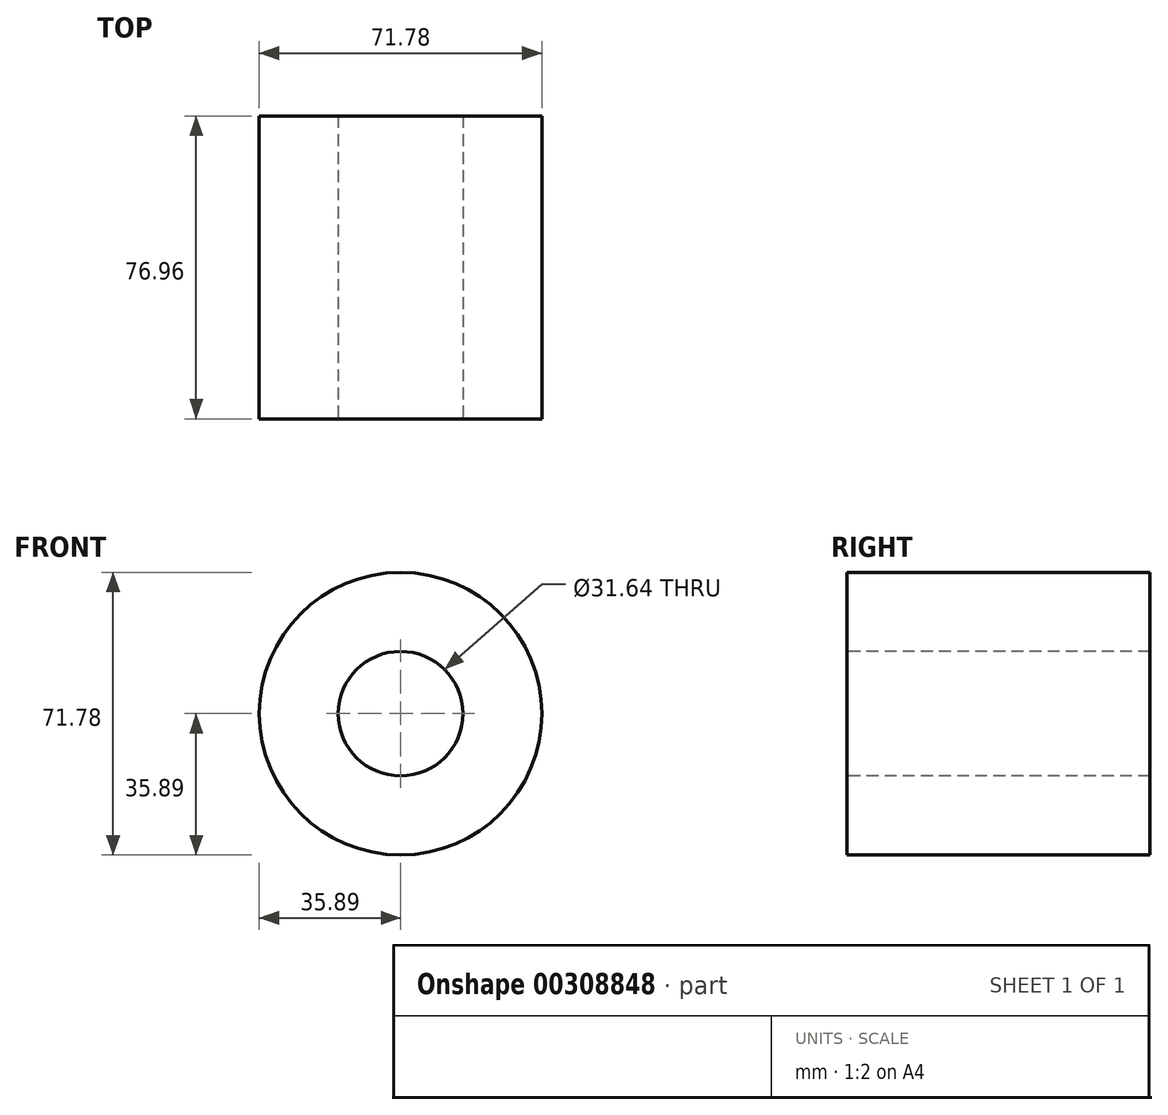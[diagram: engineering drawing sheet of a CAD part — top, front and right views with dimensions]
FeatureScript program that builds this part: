
annotation { "Feature Type Name" : "Feature", "Feature Type Description" : "" }
export const myFeature = defineFeature(function(context is Context, id is Id, definition is map)
    precondition{}
    {
        {
            var Q0;
            Q0=qCreatedBy(makeId("Front.planeOp"),FACE);
            var sketch = newSketch(context, id + "F0", { "sketchPlane" : qUnion([Q0])});
            skCircle(sketch, "E0", {"center": v(0, 0) * mm, "radius": 35.9 * mm});
            skSolve(sketch);
        }
        {
            var Q0;
            Q0=makeQuery(id+"F0.imprint","IMPRINT",FACE,{"disambiguationData":[TD([[makeQuery(id+"F0.imprint","IMPRINT",EDGE,{"derivedFrom":sQuery(id+"F0.wireOp",EDGE,"E0")}),1.0]])]});
            extrude(context, id + "F1", {"entities" : qUnion([Q0]), "depth" : 76.96 * mm});
        }
        {
            var Q0;
            Q0=makeQuery(id+"F1.opExtrude","CAP_FACE",FACE,{"disambiguationData":[OSD([sQuery(id+"F0.wireOp",EDGE,"E0")])],"isStart":false});
            var sketch = newSketch(context, id + "F2", { "sketchPlane" : qUnion([Q0])});
            skCircle(sketch, "E1", {"center": v(0, 0) * mm, "radius": 15.82 * mm});
            skSolve(sketch);
        }
        {
            var Q0;
            Q0 = qSketchRegion(id + "F2", true);
            extrude(context, id + "F3", {"entities" : qUnion([Q0]), "operationType" : NewBodyOperationType.REMOVE, "endBound" : BoundingType.UP_TO_NEXT, "oppositeDirection" : true, "depth" : 25.4 * mm});
        }
    });
